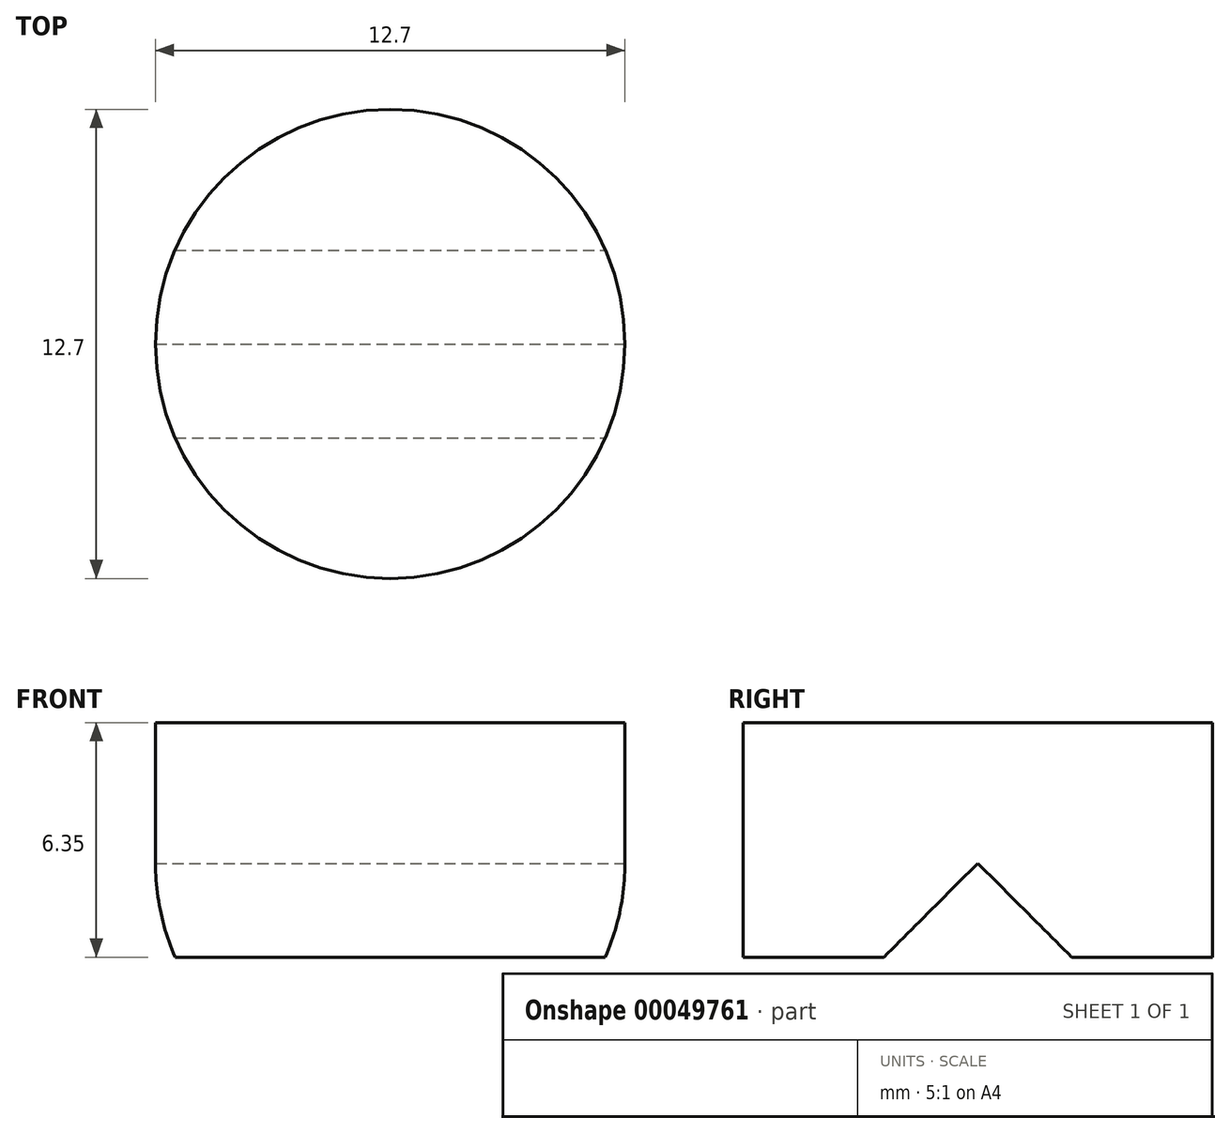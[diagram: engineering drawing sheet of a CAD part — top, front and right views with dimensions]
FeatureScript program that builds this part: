
annotation { "Feature Type Name" : "Feature", "Feature Type Description" : "" }
export const myFeature = defineFeature(function(context is Context, id is Id, definition is map)
    precondition{}
    {
        {
            var Q0;
            Q0=qCreatedBy(makeId("Top.planeOp"),FACE);
            var sketch = newSketch(context, id + "F0", { "sketchPlane" : qUnion([Q0])});
            skCircle(sketch, "E0", {"center": v(0, 0) * mm, "radius": 6.35 * mm});
            skSolve(sketch);
        }
        {
            var Q0;
            Q0=qSketchRegion(id+"F0",true);
            extrude(context, id + "F1", {"entities" : qUnion([Q0]), "depth" : 6.35 * mm});
        }
        {
            var Q0;
            Q0=qCreatedBy(makeId("Top.planeOp"),FACE);
            var sketch = newSketch(context, id + "F2", { "sketchPlane" : qUnion([Q0])});
            skCircle(sketch, "E1", {"center": v(0, 0) * mm, "radius": 1.27 * mm});
            skSolve(sketch);
        }
        {
            var Q0;
            Q0=qCreatedBy(makeId("Right.planeOp"),FACE);
            var sketch = newSketch(context, id + "F3", { "sketchPlane" : qUnion([Q0])});
            skCircle(sketch, "E2.cCircle", {"center": v(0, 0) * mm, "radius": 2.54 * mm, "construction": true});
            skLineSegment(sketch, "E2.0", {"start": v(2.54, 0) * mm, "end": v(0, -2.54) * mm});
            skLineSegment(sketch, "E2.1", {"start": v(0, -2.54) * mm, "end": v(-2.54, 0) * mm});
            skLineSegment(sketch, "E2.2", {"start": v(-2.54, 0) * mm, "end": v(0, 2.54) * mm});
            skLineSegment(sketch, "E2.3", {"start": v(0, 2.54) * mm, "end": v(2.54, 0) * mm});
            skSolve(sketch);
        }
        {
            var Q0;
            Q0=qSketchRegion(id+"F3",true);
            extrude(context, id + "F4", {"entities" : qUnion([Q0]), "operationType" : NewBodyOperationType.REMOVE, "endBound" : BoundingType.SYMMETRIC, "oppositeDirection" : true, "depth" : 25.4 * mm});
        }
    });
